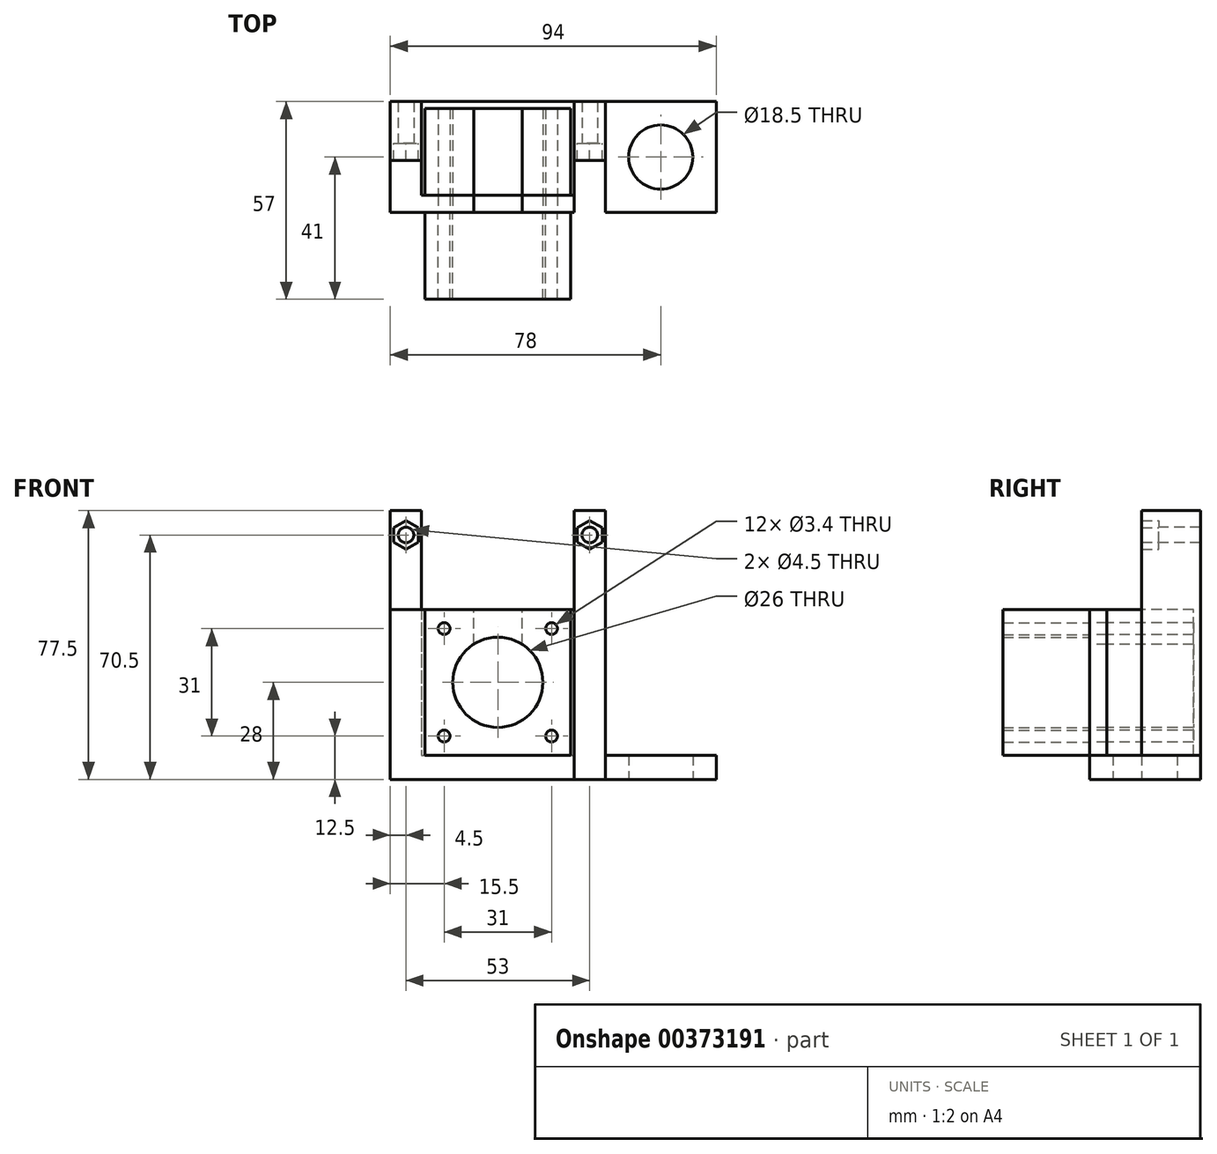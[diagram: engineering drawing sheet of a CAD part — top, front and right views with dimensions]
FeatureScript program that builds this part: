
annotation { "Feature Type Name" : "Feature", "Feature Type Description" : "" }
export const myFeature = defineFeature(function(context is Context, id is Id, definition is map)
    precondition{}
    {
        {
            assignVariable(context, id + "F0", {"name" : "MotorLength", "anyValue" : 25});
        }
        {
            var Q0;
            Q0=qCreatedBy(makeId("Front.planeOp"),FACE);
            var sketch = newSketch(context, id + "F1", { "sketchPlane" : qUnion([Q0])});
            skCircle(sketch, "E0", {"center": v(0, 0) * mm, "radius": 2.25 * mm});
            skCircle(sketch, "E1", {"center": v(-31.5, 49.5) * mm, "radius": 2.25 * mm});
            skCircle(sketch, "E2", {"center": v(21.5, 49.5) * mm, "radius": 2.25 * mm});
            skPoint(sketch, "E3", {"position": v(-36, 56.5) * mm});
            skPoint(sketch, "E4", {"position": v(-27, 56.5) * mm});
            skPoint(sketch, "E5", {"position": v(-27, -14) * mm});
            skLineSegment(sketch, "E6", {"start": v(-36, 56.5) * mm, "end": v(-27, 56.5) * mm});
            skLineSegment(sketch, "E7", {"start": v(-27, 56.5) * mm, "end": v(-27, -14) * mm});
            skLineSegment(sketch, "E8", {"start": v(-27, -14) * mm, "end": v(17, -14) * mm});
            skLineSegment(sketch, "E9", {"start": v(17, -14) * mm, "end": v(17, 56.5) * mm});
            skLineSegment(sketch, "E10", {"start": v(17, 56.5) * mm, "end": v(26, 56.5) * mm});
            skPoint(sketch, "E11", {"position": v(-36, -21) * mm});
            skLineSegment(sketch, "E12", {"start": v(-36, 56.5) * mm, "end": v(-36, -21) * mm});
            skLineSegment(sketch, "E13", {"start": v(-36, -21) * mm, "end": v(26, -21) * mm});
            skLineSegment(sketch, "E14", {"start": v(26, 56.5) * mm, "end": v(26, -21) * mm});
            skSolve(sketch);
        }
        {
            var Q0;
            Q0=makeQuery(id+"F1.imprint","IMPRINT",FACE,{"disambiguationData":[TD([[makeQuery(id+"F1.imprint","IMPRINT",EDGE,{"derivedFrom":sQuery(id+"F1.wireOp",EDGE,"E1")}),-1.0]])]});
            extrude(context, id + "F2", {"entities" : qUnion([Q0]), "oppositeDirection" : true, "depth" : 12 * mm});
        }
        {
            var Q0;
            Q0=makeQuery(id+"F2.opExtrude","CAP_FACE",FACE,{"disambiguationData":[OSD([sQuery(id+"F1.wireOp",EDGE,"E1"),sQuery(id+"F1.wireOp",EDGE,"E2"),sQuery(id+"F1.wireOp",EDGE,"E6"),sQuery(id+"F1.wireOp",EDGE,"E7"),sQuery(id+"F1.wireOp",EDGE,"E8"),sQuery(id+"F1.wireOp",EDGE,"E9"),sQuery(id+"F1.wireOp",EDGE,"E10"),sQuery(id+"F1.wireOp",EDGE,"E12"),sQuery(id+"F1.wireOp",EDGE,"E13"),sQuery(id+"F1.wireOp",EDGE,"E14")])],"isStart":true});
            var sketch = newSketch(context, id + "F3", { "sketchPlane" : qUnion([Q0])});
            skCircle(sketch, "E15.cCircle", {"center": v(-31.5, 49.5) * mm, "radius": 3.6 * mm, "construction": true});
            skLineSegment(sketch, "E15.0", {"start": v(-27.9, 51.58) * mm, "end": v(-27.9, 47.42) * mm});
            skLineSegment(sketch, "E15.1", {"start": v(-27.9, 47.42) * mm, "end": v(-31.5, 45.34) * mm});
            skLineSegment(sketch, "E15.2", {"start": v(-31.5, 45.34) * mm, "end": v(-35.1, 47.42) * mm});
            skLineSegment(sketch, "E15.3", {"start": v(-35.1, 47.42) * mm, "end": v(-35.1, 51.58) * mm});
            skLineSegment(sketch, "E15.4", {"start": v(-35.1, 51.58) * mm, "end": v(-31.5, 53.66) * mm});
            skLineSegment(sketch, "E15.5", {"start": v(-31.5, 53.66) * mm, "end": v(-27.9, 51.58) * mm});
            skPoint(sketch, "E15.0.midPoint", {"position": v(-27.9, 49.5) * mm});
            skCircle(sketch, "E16.cCircle", {"center": v(21.5, 49.5) * mm, "radius": 3.6 * mm, "construction": true});
            skLineSegment(sketch, "E16.0", {"start": v(25.1, 51.58) * mm, "end": v(25.1, 47.42) * mm});
            skLineSegment(sketch, "E16.1", {"start": v(25.1, 47.42) * mm, "end": v(21.5, 45.34) * mm});
            skLineSegment(sketch, "E16.2", {"start": v(21.5, 45.34) * mm, "end": v(17.9, 47.42) * mm});
            skLineSegment(sketch, "E16.3", {"start": v(17.9, 47.42) * mm, "end": v(17.9, 51.58) * mm});
            skLineSegment(sketch, "E16.4", {"start": v(17.9, 51.58) * mm, "end": v(21.5, 53.66) * mm});
            skLineSegment(sketch, "E16.5", {"start": v(21.5, 53.66) * mm, "end": v(25.1, 51.58) * mm});
            skPoint(sketch, "E16.0.midPoint", {"position": v(25.1, 49.5) * mm});
            skSolve(sketch);
        }
        {
            var Q0;
            Q0=makeQuery(id+"F3.imprint","IMPRINT",FACE,{"disambiguationData":[TD([[makeQuery(id+"F3.imprint","IMPRINT",EDGE,{"derivedFrom":sQuery(id+"F3.wireOp",EDGE,"E15.0")}),1.0]])]});
            extrude(context, id + "F4", {"entities" : qUnion([Q0]), "operationType" : NewBodyOperationType.ADD, "depth" : 5 * mm});
        }
        {
            var Q0;
            {var subQ0=sQuery(id+"F1.wireOp",EDGE,"E8");Q0=makeQuery(id+"F4.boolean.opBoolean","MERGE",FACE,{"derivedFrom":[makeQuery(id+"F2.opExtrude","SWEPT_FACE",FACE,{"disambiguationData":[OSD([subQ0])]}),makeQuery(id+"F4.opExtrude","SWEPT_FACE",FACE,{"disambiguationData":[OSD([subQ0])]})]});}
            var sketch = newSketch(context, id + "F5", { "sketchPlane" : qUnion([Q0])});
            skLineSegment(sketch, "E17.0", {"start": v(-27, 12) * mm, "end": v(17, 12) * mm});
            skPoint(sketch, "E18.oppositeSnap0", {"position": v(17, 3.5) * mm});
            skLineSegment(sketch, "E18.top", {"start": v(-27, -15) * mm, "end": v(17, -15) * mm});
            skLineSegment(sketch, "E18.left", {"start": v(-27, 12) * mm, "end": v(-27, -15) * mm});
            skLineSegment(sketch, "E18.right", {"start": v(17, 12) * mm, "end": v(17, -15) * mm});
            skLineSegment(sketch, "E19.top", {"start": v(-27, -20) * mm, "end": v(17, -20) * mm});
            skLineSegment(sketch, "E19.left", {"start": v(-27, -15) * mm, "end": v(-27, -20) * mm});
            skLineSegment(sketch, "E19.right", {"start": v(17, -15) * mm, "end": v(17, -20) * mm});
            skLineSegment(sketch, "E20.0", {"start": v(17, -5) * mm, "end": v(26, -5) * mm});
            skLineSegment(sketch, "E21.bottom", {"start": v(26, -5) * mm, "end": v(17, -5) * mm});
            skLineSegment(sketch, "E21.top", {"start": v(26, -20) * mm, "end": v(17, -20) * mm});
            skLineSegment(sketch, "E21.left", {"start": v(26, -5) * mm, "end": v(26, -20) * mm});
            skLineSegment(sketch, "E21.right", {"start": v(17, -5) * mm, "end": v(17, -20) * mm});
            skLineSegment(sketch, "E22.0", {"start": v(-36, -5) * mm, "end": v(-27, -5) * mm});
            skLineSegment(sketch, "E23.top", {"start": v(-36, -20) * mm, "end": v(-27, -20) * mm});
            skLineSegment(sketch, "E23.left", {"start": v(-36, -5) * mm, "end": v(-36, -20) * mm});
            skLineSegment(sketch, "E23.right", {"start": v(-27, -5) * mm, "end": v(-27, -20) * mm});
            skSolve(sketch);
        }
        {
            var Q0;
            {var subQ0=sQuery(id+"F5.wireOp",EDGE,"E18.top");Q0=makeQuery(id+"F5.imprint","IMPRINT",FACE,{"disambiguationData":[TD([[makeQuery(id+"F5.imprint","IMPRINT",EDGE,{"derivedFrom":subQ0}),1.0]])]});}
            var Q1;
            {var subQ0=sQuery(id+"F5.wireOp",EDGE,"E18.top");Q1=makeQuery(id+"F5.imprint","IMPRINT",FACE,{"disambiguationData":[TD([[makeQuery(id+"F5.imprint","IMPRINT",EDGE,{"derivedFrom":subQ0}),-1.0]])]});}
            var Q2;
            {var subQ1=sQuery(id+"F5.wireOp",EDGE,"E22.0");Q2=makeQuery(id+"F5.imprint","IMPRINT",FACE,{"disambiguationData":[TD([[makeQuery(id+"F5.imprint","IMPRINT",EDGE,{"derivedFrom":subQ1}),-1.0]])]});}
            var Q3;
            {var subQ1=sQuery(id+"F5.wireOp",EDGE,"E21.bottom");Q3=makeQuery(id+"F5.imprint","IMPRINT",FACE,{"disambiguationData":[TD([[makeQuery(id+"F5.imprint","IMPRINT",EDGE,{"derivedFrom":subQ1}),1.0]])]});}
            var Q4;
            {var subQ0=sQuery(id+"F1.wireOp",EDGE,"E13");Q4=makeQuery(id+"F4.boolean.opBoolean","MERGE",FACE,{"derivedFrom":[makeQuery(id+"F2.opExtrude","SWEPT_FACE",FACE,{"disambiguationData":[OSD([subQ0])]}),makeQuery(id+"F4.opExtrude","SWEPT_FACE",FACE,{"disambiguationData":[OSD([subQ0])]})]});}
            extrude(context, id + "F6", {"entities" : qUnion([Q0, Q1, Q2, Q3]), "operationType" : NewBodyOperationType.ADD, "endBound" : BoundingType.UP_TO_SURFACE, "oppositeDirection" : true, "endBoundEntityFace" : qUnion([Q4]), "depth" : 25 * mm});
        }
        {
            var Q0;
            {var subQ0=sQuery(id+"F5.wireOp",EDGE,"E18.top");Q0=makeQuery(id+"F5.imprint","IMPRINT",FACE,{"disambiguationData":[TD([[makeQuery(id+"F5.imprint","IMPRINT",EDGE,{"derivedFrom":subQ0}),-1.0]])]});}
            var Q1;
            {var subQ1=sQuery(id+"F5.wireOp",EDGE,"E22.0");Q1=makeQuery(id+"F5.imprint","IMPRINT",FACE,{"disambiguationData":[TD([[makeQuery(id+"F5.imprint","IMPRINT",EDGE,{"derivedFrom":subQ1}),-1.0]])]});}
            var Q2;
            {var subQ1=sQuery(id+"F5.wireOp",EDGE,"E21.bottom");Q2=makeQuery(id+"F5.imprint","IMPRINT",FACE,{"disambiguationData":[TD([[makeQuery(id+"F5.imprint","IMPRINT",EDGE,{"derivedFrom":subQ1}),1.0]])]});}
            extrude(context, id + "F7", {"entities" : qUnion([Q0, Q1, Q2]), "operationType" : NewBodyOperationType.ADD, "depth" : 42 * mm});
        }
        {
            var Q0;
            {var subQ0=sQuery(id+"F5.wireOp",EDGE,"E23.top");var subQ1=sQuery(id+"F5.wireOp",EDGE,"E21.top");var subQ2=sQuery(id+"F5.wireOp",EDGE,"E19.top");Q0=makeQuery(id+"F7.boolean.opBoolean","MERGE",FACE,{"derivedFrom":[makeQuery(id+"F6.opExtrude","SWEPT_FACE",FACE,{"disambiguationData":[OSD([subQ2,subQ1,subQ0])]}),makeQuery(id+"F7.opExtrude","SWEPT_FACE",FACE,{"disambiguationData":[OSD([subQ2,subQ1,subQ0])]})]});}
            var sketch = newSketch(context, id + "F8", { "sketchPlane" : qUnion([Q0])});
            skLineSegment(sketch, "E24.0", {"start": v(-26, -14) * mm, "end": v(16, -14) * mm});
            skPoint(sketch, "E25", {"position": v(-5, -14) * mm});
            skPoint(sketch, "E26", {"position": v(-26, -14) * mm});
            skPoint(sketch, "E27", {"position": v(16, -14) * mm});
            skPoint(sketch, "E28.orphan", {"position": v(-27, -14) * mm});
            skPoint(sketch, "E29.orphan", {"position": v(17, -14) * mm});
            skPoint(sketch, "E30", {"position": v(-26, 28) * mm});
            skPoint(sketch, "E31", {"position": v(16, 28) * mm});
            skLineSegment(sketch, "E32", {"start": v(-26, 28) * mm, "end": v(16, -14) * mm, "construction": true});
            skLineSegment(sketch, "E33", {"start": v(-26, -14) * mm, "end": v(16, 28) * mm, "construction": true});
            skPoint(sketch, "E34", {"position": v(-5, 7) * mm});
            skCircle(sketch, "E35", {"center": v(-5, 7) * mm, "radius": 13 * mm});
            skCircle(sketch, "E36", {"center": v(-20.5, 22.5) * mm, "radius": 1.7 * mm});
            skCircle(sketch, "E37.1.0", {"center": v(-20.5, -8.5) * mm, "radius": 1.7 * mm});
            skCircle(sketch, "E37.2.0", {"center": v(10.5, -8.5) * mm, "radius": 1.7 * mm});
            skCircle(sketch, "E37.3.0", {"center": v(10.5, 22.5) * mm, "radius": 1.7 * mm});
            skSolve(sketch);
        }
        {
            var Q0;
            Q0=makeQuery(id+"F8.imprint","IMPRINT",FACE,{"disambiguationData":[TD([[makeQuery(id+"F8.imprint","IMPRINT",EDGE,{"derivedFrom":sQuery(id+"F8.wireOp",EDGE,"E36")}),1.0]])]});
            var Q1;
            Q1=makeQuery(id+"F8.imprint","IMPRINT",FACE,{"disambiguationData":[TD([[makeQuery(id+"F8.imprint","IMPRINT",EDGE,{"derivedFrom":sQuery(id+"F8.wireOp",EDGE,"E35")}),1.0]])]});
            var Q2;
            Q2=makeQuery(id+"F8.imprint","IMPRINT",FACE,{"disambiguationData":[TD([[makeQuery(id+"F8.imprint","IMPRINT",EDGE,{"derivedFrom":sQuery(id+"F8.wireOp",EDGE,"E37.1.0")}),1.0]])]});
            var Q3;
            Q3=makeQuery(id+"F8.imprint","IMPRINT",FACE,{"disambiguationData":[TD([[makeQuery(id+"F8.imprint","IMPRINT",EDGE,{"derivedFrom":sQuery(id+"F8.wireOp",EDGE,"E37.2.0")}),1.0]])]});
            var Q4;
            Q4=makeQuery(id+"F8.imprint","IMPRINT",FACE,{"disambiguationData":[TD([[makeQuery(id+"F8.imprint","IMPRINT",EDGE,{"derivedFrom":sQuery(id+"F8.wireOp",EDGE,"E37.3.0")}),1.0]])]});
            var Q5;
            Q5=makeQuery(id+"F7.opExtrude","SWEPT_FACE",FACE,{"disambiguationData":[OSD([sQuery(id+"F5.wireOp",EDGE,"E18.top")])]});
            extrude(context, id + "F9", {"entities" : qUnion([Q0, Q1, Q2, Q3, Q4]), "operationType" : NewBodyOperationType.REMOVE, "endBound" : BoundingType.UP_TO_SURFACE, "oppositeDirection" : true, "endBoundEntityFace" : qUnion([Q5]), "depth" : 25 * mm});
        }
        {
            var Q0;
            Q0=makeQuery(id+"F7.opExtrude","CAP_FACE",FACE,{"disambiguationData":[OSD([sQuery(id+"F5.wireOp",EDGE,"E18.top"),sQuery(id+"F5.wireOp",EDGE,"E19.top"),sQuery(id+"F5.wireOp",EDGE,"E21.bottom"),sQuery(id+"F5.wireOp",EDGE,"E21.top"),sQuery(id+"F5.wireOp",EDGE,"E21.left"),sQuery(id+"F5.wireOp",EDGE,"E21.right"),sQuery(id+"F5.wireOp",EDGE,"E22.0"),sQuery(id+"F5.wireOp",EDGE,"E23.top"),sQuery(id+"F5.wireOp",EDGE,"E23.left"),sQuery(id+"F5.wireOp",EDGE,"E23.right")])],"isStart":false});
            var sketch = newSketch(context, id + "F10", { "sketchPlane" : qUnion([Q0])});
            skLineSegment(sketch, "E38", {"start": v(-5, -20) * mm, "end": v(-5, -15) * mm, "construction": true});
            skLineSegment(sketch, "E39", {"start": v(-5, -15) * mm, "end": v(-12, -15) * mm});
            skLineSegment(sketch, "E40", {"start": v(-5, -15) * mm, "end": v(2, -15) * mm});
            skLineSegment(sketch, "E41.bottom", {"start": v(-12, -15) * mm, "end": v(2, -15) * mm});
            skLineSegment(sketch, "E41.top", {"start": v(-12, -20) * mm, "end": v(2, -20) * mm});
            skLineSegment(sketch, "E41.left", {"start": v(-12, -15) * mm, "end": v(-12, -20) * mm});
            skLineSegment(sketch, "E41.right", {"start": v(2, -15) * mm, "end": v(2, -20) * mm});
            skSolve(sketch);
        }
        {
            var Q0;
            Q0=makeQuery(id+"F10.imprint","IMPRINT",FACE,{"disambiguationData":[TD([[makeQuery(id+"F10.imprint","IMPRINT",EDGE,{"derivedFrom":sQuery(id+"F10.wireOp",EDGE,"E41.top")}),1.0]])]});
            var Q1;
            Q1=makeQuery(id+"F9.boolean.opBoolean","COPY",FACE,{"derivedFrom":makeQuery(id+"F9.opExtrude","SWEPT_FACE",FACE,{"disambiguationData":[OSD([sQuery(id+"F8.wireOp",EDGE,"E35")])]})});
            extrude(context, id + "F11", {"entities" : qUnion([Q0]), "operationType" : NewBodyOperationType.REMOVE, "endBound" : BoundingType.UP_TO_SURFACE, "oppositeDirection" : true, "endBoundEntityFace" : qUnion([Q1]), "depth" : 25 * mm});
        }
        {
            var Q0;
            Q0=makeQuery(id+"F7.opExtrude","SWEPT_FACE",FACE,{"disambiguationData":[OSD([sQuery(id+"F5.wireOp",EDGE,"E18.top")])]});
            var sketch = newSketch(context, id + "F12", { "sketchPlane" : qUnion([Q0])});
            skLineSegment(sketch, "E42.0", {"start": v(26, -14) * mm, "end": v(-16, -14) * mm});
            skLineSegment(sketch, "E43", {"start": v(-16, -14) * mm, "end": v(-16, 28) * mm});
            skLineSegment(sketch, "E44", {"start": v(-16, 28) * mm, "end": v(26, 28) * mm});
            skLineSegment(sketch, "E45", {"start": v(26, 28) * mm, "end": v(26, -14) * mm});
            skSolve(sketch);
        }
        {
            var Q0;
            Q0=makeQuery(id+"F12.imprint","IMPRINT",FACE,{"disambiguationData":[TD([[makeQuery(id+"F12.imprint","IMPRINT",EDGE,{"derivedFrom":sQuery(id+"F12.wireOp",EDGE,"E42.0")}),-1.0]])]});
            var Q1;
            {var subQ2=sQuery(id+"F5.wireOp",EDGE,"E18.top");Q1=makeQuery(id+"F12.imprint","IMPRINT",FACE,{"disambiguationData":[TD([[makeQuery(id+"F12.imprint","IMPRINT",EDGE,{"derivedFrom":makeQuery(id+"F9.boolean.opBoolean","COPY",EDGE,{"derivedFrom":makeQuery(id+"F9.opExtrude","TWEAK_EDGE",EDGE,{"derivedFrom":[makeQuery(id+"F7.opExtrude","SWEPT_FACE",FACE,{"disambiguationData":[OSD([subQ2])]}),makeQuery(id+"F8.imprint","IMPRINT",EDGE,{"derivedFrom":sQuery(id+"F8.wireOp",EDGE,"E35")})]})})}),-1.0]])]});}
            var Q2;
            Q2=makeQuery(id+"F12.imprint","IMPRINT",FACE,{"disambiguationData":[TD([[makeQuery(id+"F12.imprint","IMPRINT",EDGE,{"derivedFrom":makeQuery(id+"F9.boolean.opBoolean","COPY",EDGE,{"derivedFrom":makeQuery(id+"F9.opExtrude","TWEAK_EDGE",EDGE,{"derivedFrom":[makeQuery(id+"F7.opExtrude","SWEPT_FACE",FACE,{"disambiguationData":[OSD([sQuery(id+"F5.wireOp",EDGE,"E18.top")])]}),makeQuery(id+"F8.imprint","IMPRINT",EDGE,{"derivedFrom":sQuery(id+"F8.wireOp",EDGE,"E36")})]})})}),-1.0]])]});
            var Q3;
            Q3=makeQuery(id+"F12.imprint","IMPRINT",FACE,{"disambiguationData":[TD([[makeQuery(id+"F12.imprint","IMPRINT",EDGE,{"derivedFrom":makeQuery(id+"F9.boolean.opBoolean","COPY",EDGE,{"derivedFrom":makeQuery(id+"F9.opExtrude","TWEAK_EDGE",EDGE,{"derivedFrom":[makeQuery(id+"F7.opExtrude","SWEPT_FACE",FACE,{"disambiguationData":[OSD([sQuery(id+"F5.wireOp",EDGE,"E18.top")])]}),makeQuery(id+"F8.imprint","IMPRINT",EDGE,{"derivedFrom":sQuery(id+"F8.wireOp",EDGE,"E37.3.0")})]})})}),-1.0]])]});
            var Q4;
            Q4=makeQuery(id+"F12.imprint","IMPRINT",FACE,{"disambiguationData":[TD([[makeQuery(id+"F12.imprint","IMPRINT",EDGE,{"derivedFrom":makeQuery(id+"F9.boolean.opBoolean","COPY",EDGE,{"derivedFrom":makeQuery(id+"F9.opExtrude","TWEAK_EDGE",EDGE,{"derivedFrom":[makeQuery(id+"F7.opExtrude","SWEPT_FACE",FACE,{"disambiguationData":[OSD([sQuery(id+"F5.wireOp",EDGE,"E18.top")])]}),makeQuery(id+"F8.imprint","IMPRINT",EDGE,{"derivedFrom":sQuery(id+"F8.wireOp",EDGE,"E37.2.0")})]})})}),-1.0]])]});
            var Q5;
            Q5=makeQuery(id+"F12.imprint","IMPRINT",FACE,{"disambiguationData":[TD([[makeQuery(id+"F12.imprint","IMPRINT",EDGE,{"derivedFrom":makeQuery(id+"F9.boolean.opBoolean","COPY",EDGE,{"derivedFrom":makeQuery(id+"F9.opExtrude","TWEAK_EDGE",EDGE,{"derivedFrom":[makeQuery(id+"F7.opExtrude","SWEPT_FACE",FACE,{"disambiguationData":[OSD([sQuery(id+"F5.wireOp",EDGE,"E18.top")])]}),makeQuery(id+"F8.imprint","IMPRINT",EDGE,{"derivedFrom":sQuery(id+"F8.wireOp",EDGE,"E37.1.0")})]})})}),-1.0]])]});
            extrude(context, id + "F13", {"entities" : qUnion([Q0, Q1, Q2, Q3, Q4, Q5]), "depth" : (getVariable(context, 'MotorLength')) * mm});
        }
        {
            var Q0;
            Q0=makeQuery(id+"F8.imprint","IMPRINT",FACE,{"disambiguationData":[TD([[makeQuery(id+"F8.imprint","IMPRINT",EDGE,{"derivedFrom":sQuery(id+"F8.wireOp",EDGE,"E35")}),-1.0]])]});
            var sketch = newSketch(context, id + "F14", { "sketchPlane" : qUnion([Q0])});
            skLineSegment(sketch, "E46.0", {"start": v(-26, 28) * mm, "end": v(16, -14) * mm, "construction": true});
            skLineSegment(sketch, "E47.0", {"start": v(-26, -14) * mm, "end": v(16, 28) * mm, "construction": true});
            skLineSegment(sketch, "E48.bottom", {"start": v(-26, 28) * mm, "end": v(16, 28) * mm});
            skLineSegment(sketch, "E48.top", {"start": v(-26, -14) * mm, "end": v(16, -14) * mm});
            skLineSegment(sketch, "E48.left", {"start": v(-26, 28) * mm, "end": v(-26, -14) * mm});
            skLineSegment(sketch, "E48.right", {"start": v(16, 28) * mm, "end": v(16, -14) * mm});
            skSolve(sketch);
        }
        {
            var Q0;
            Q0=makeQuery(id+"F14.imprint","IMPRINT",FACE,{"disambiguationData":[TD([[makeQuery(id+"F14.imprint","IMPRINT",EDGE,{"derivedFrom":sQuery(id+"F14.wireOp",EDGE,"E48.bottom")}),-1.0]])]});
            var Q1;
            Q1=makeQuery(id+"F8.imprint","IMPRINT",FACE,{"disambiguationData":[TD([[makeQuery(id+"F8.imprint","IMPRINT",EDGE,{"derivedFrom":sQuery(id+"F8.wireOp",EDGE,"E36")}),1.0]])]});
            var Q2;
            Q2=makeQuery(id+"F8.imprint","IMPRINT",FACE,{"disambiguationData":[TD([[makeQuery(id+"F8.imprint","IMPRINT",EDGE,{"derivedFrom":sQuery(id+"F8.wireOp",EDGE,"E35")}),1.0]])]});
            var Q3;
            Q3=makeQuery(id+"F8.imprint","IMPRINT",FACE,{"disambiguationData":[TD([[makeQuery(id+"F8.imprint","IMPRINT",EDGE,{"derivedFrom":sQuery(id+"F8.wireOp",EDGE,"E37.1.0")}),1.0]])]});
            var Q4;
            Q4=makeQuery(id+"F8.imprint","IMPRINT",FACE,{"disambiguationData":[TD([[makeQuery(id+"F8.imprint","IMPRINT",EDGE,{"derivedFrom":sQuery(id+"F8.wireOp",EDGE,"E37.3.0")}),1.0]])]});
            var Q5;
            Q5=makeQuery(id+"F8.imprint","IMPRINT",FACE,{"disambiguationData":[TD([[makeQuery(id+"F8.imprint","IMPRINT",EDGE,{"derivedFrom":sQuery(id+"F8.wireOp",EDGE,"E37.2.0")}),1.0]])]});
            extrude(context, id + "F15", {"entities" : qUnion([Q0, Q1, Q2, Q3, Q4, Q5]), "depth" : 25 * mm});
        }
        {
            var Q0;
            {var subQ0=sQuery(id+"F1.wireOp",EDGE,"E13");Q0=makeQuery(id+"F6.boolean.opBoolean","MERGE",FACE,{"derivedFrom":[makeQuery(id+"F4.boolean.opBoolean","MERGE",FACE,{"derivedFrom":[makeQuery(id+"F2.opExtrude","SWEPT_FACE",FACE,{"disambiguationData":[OSD([subQ0])]}),makeQuery(id+"F4.opExtrude","SWEPT_FACE",FACE,{"disambiguationData":[OSD([subQ0])]})]}),makeQuery(id+"F6.opExtrude","CAP_FACE",FACE,{"disambiguationData":[OSD([subQ0])],"isStart":false})]});}
            var sketch = newSketch(context, id + "F16", { "sketchPlane" : qUnion([Q0])});
            skLineSegment(sketch, "E49.bottom", {"start": v(26, -12) * mm, "end": v(58, -12) * mm});
            skLineSegment(sketch, "E49.top", {"start": v(26, 20) * mm, "end": v(58, 20) * mm});
            skLineSegment(sketch, "E49.left", {"start": v(26, -12) * mm, "end": v(26, 20) * mm});
            skLineSegment(sketch, "E49.right", {"start": v(58, -12) * mm, "end": v(58, 20) * mm});
            skCircle(sketch, "E50", {"center": v(42, 4) * mm, "radius": 9.25 * mm});
            skPoint(sketch, "E50.centerSnap0", {"position": v(42, -12) * mm});
            skPoint(sketch, "E50.centerSnap1", {"position": v(26, 4) * mm});
            skLineSegment(sketch, "E51.0", {"start": v(-26, 45) * mm, "end": v(-26, 20) * mm, "construction": true});
            skLineSegment(sketch, "E52.0", {"start": v(-26, 20) * mm, "end": v(16, 20) * mm, "construction": true});
            skLineSegment(sketch, "E53", {"start": v(-5, 20) * mm, "end": v(-5, 45) * mm, "construction": true});
            skLineSegment(sketch, "E54", {"start": v(6.1, 20) * mm, "end": v(6.1, 45) * mm, "construction": true});
            skPoint(sketch, "E55", {"position": v(6.1, 32.5) * mm});
            skSolve(sketch);
        }
        {
            var Q0;
            Q0=qSketchRegion(id+"F16",true);
            var Q1;
            {var subQ0=sQuery(id+"F1.wireOp",EDGE,"E8");Q1=makeQuery(id+"F6.boolean.opBoolean","MERGE",FACE,{"derivedFrom":[makeQuery(id+"F4.boolean.opBoolean","MERGE",FACE,{"derivedFrom":[makeQuery(id+"F2.opExtrude","SWEPT_FACE",FACE,{"disambiguationData":[OSD([subQ0])]}),makeQuery(id+"F4.opExtrude","SWEPT_FACE",FACE,{"disambiguationData":[OSD([subQ0])]})]}),makeQuery(id+"F6.opExtrude","CAP_FACE",FACE,{"disambiguationData":[OSD([subQ0,sQuery(id+"F5.wireOp",EDGE,"E19.top"),sQuery(id+"F5.wireOp",EDGE,"E21.bottom"),sQuery(id+"F5.wireOp",EDGE,"E21.top"),sQuery(id+"F5.wireOp",EDGE,"E21.left"),sQuery(id+"F5.wireOp",EDGE,"E22.0"),sQuery(id+"F5.wireOp",EDGE,"E23.top"),sQuery(id+"F5.wireOp",EDGE,"E23.left")])],"isStart":true})]});}
            extrude(context, id + "F17", {"entities" : qUnion([Q0]), "endBound" : BoundingType.UP_TO_SURFACE, "oppositeDirection" : true, "endBoundEntityFace" : qUnion([Q1]), "depth" : 25 * mm});
        }
    });
